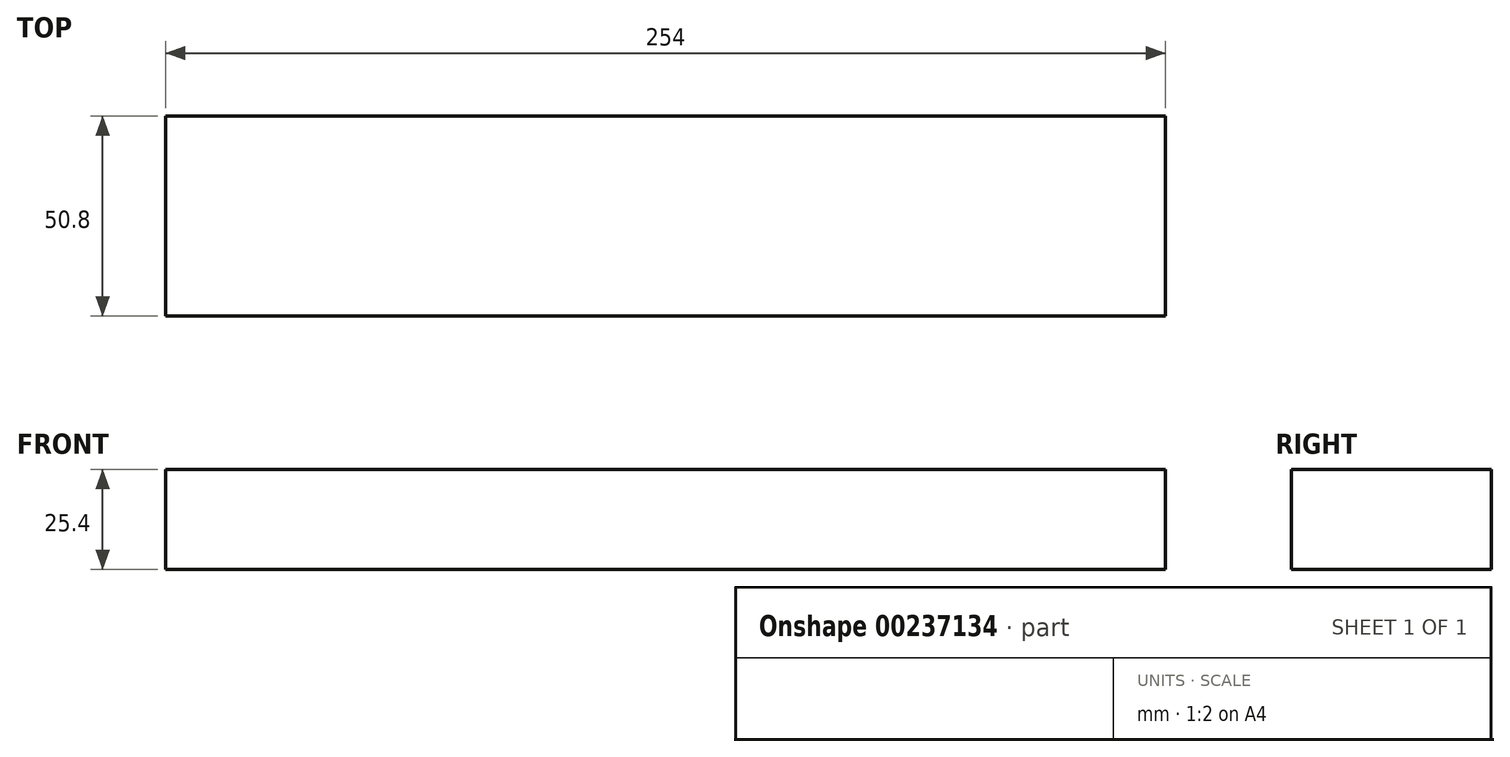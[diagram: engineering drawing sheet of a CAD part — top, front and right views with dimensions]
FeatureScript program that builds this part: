
annotation { "Feature Type Name" : "Feature", "Feature Type Description" : "" }
export const myFeature = defineFeature(function(context is Context, id is Id, definition is map)
    precondition{}
    {
        {
            var Q0;
            Q0=qCreatedBy(makeId("Top.planeOp"),FACE);
            var sketch = newSketch(context, id + "F0", { "sketchPlane" : qUnion([Q0])});
            skLineSegment(sketch, "E0.bottom", {"start": v(0, 0) * mm, "end": v(254, 0) * mm});
            skLineSegment(sketch, "E0.top", {"start": v(0, 50.8) * mm, "end": v(254, 50.8) * mm});
            skLineSegment(sketch, "E0.left", {"start": v(0, 0) * mm, "end": v(0, 50.8) * mm});
            skLineSegment(sketch, "E0.right", {"start": v(254, 0) * mm, "end": v(254, 50.8) * mm});
            skSolve(sketch);
        }
        {
            var Q0;
            Q0 = qSketchRegion(id + "F0", true);
            extrude(context, id + "F1", {"entities" : qUnion([Q0]), "depth" : 25.4 * mm});
        }
    });
